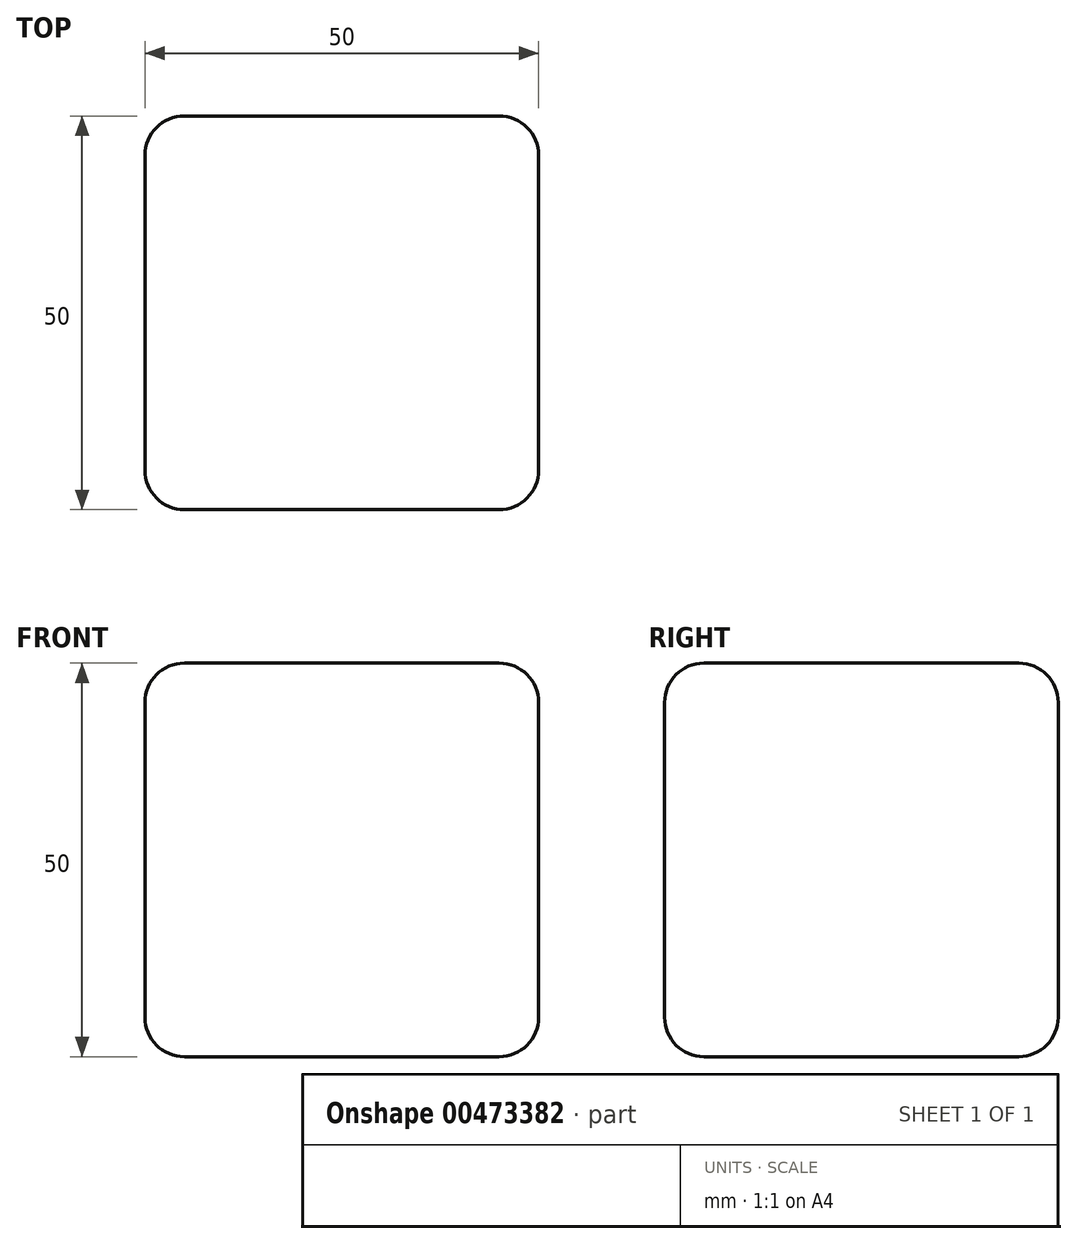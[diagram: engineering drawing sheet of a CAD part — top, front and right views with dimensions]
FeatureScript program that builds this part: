
annotation { "Feature Type Name" : "Feature", "Feature Type Description" : "" }
export const myFeature = defineFeature(function(context is Context, id is Id, definition is map)
    precondition{}
    {
        {
            var Q0;
            Q0=qCreatedBy(makeId("Front.planeOp"),FACE);
            var sketch = newSketch(context, id + "F0", { "sketchPlane" : qUnion([Q0])});
            skLineSegment(sketch, "E0.bottom", {"start": v(0, 0) * mm, "end": v(-50, 0) * mm});
            skLineSegment(sketch, "E0.top", {"start": v(0, 50) * mm, "end": v(-50, 50) * mm});
            skLineSegment(sketch, "E0.left", {"start": v(0, 0) * mm, "end": v(0, 50) * mm});
            skLineSegment(sketch, "E0.right", {"start": v(-50, 0) * mm, "end": v(-50, 50) * mm});
            skSolve(sketch);
        }
        {
            var Q0;
            Q0 = qSketchRegion(id + "F0", true);
            extrude(context, id + "F1", {"entities" : qUnion([Q0]), "depth" : 50 * mm});
        }
        {
            var Q0;
            Q0=makeQuery(id+"F1.opExtrude","SWEPT_EDGE",EDGE,{"disambiguationData":[OSD([sQuery(id+"F0.wireOp",EDGE,"E0.top"),sQuery(id+"F0.wireOp",EDGE,"E0.right")])]});
            var Q1;
            Q1=makeQuery(id+"F1.opExtrude","CAP_EDGE",EDGE,{"disambiguationData":[OSD([sQuery(id+"F0.wireOp",EDGE,"E0.top")])],"isStart":true});
            var Q2;
            Q2=makeQuery(id+"F1.opExtrude","SWEPT_EDGE",EDGE,{"disambiguationData":[OSD([sQuery(id+"F0.wireOp",EDGE,"E0.top"),sQuery(id+"F0.wireOp",EDGE,"E0.left")])]});
            var Q3;
            Q3=makeQuery(id+"F1.opExtrude","CAP_EDGE",EDGE,{"disambiguationData":[OSD([sQuery(id+"F0.wireOp",EDGE,"E0.top")])],"isStart":false});
            var Q4;
            Q4=makeQuery(id+"F1.opExtrude","CAP_EDGE",EDGE,{"disambiguationData":[OSD([sQuery(id+"F0.wireOp",EDGE,"E0.left")])],"isStart":false});
            var Q5;
            Q5=makeQuery(id+"F1.opExtrude","CAP_EDGE",EDGE,{"disambiguationData":[OSD([sQuery(id+"F0.wireOp",EDGE,"E0.left")])],"isStart":true});
            var Q6;
            Q6=makeQuery(id+"F1.opExtrude","SWEPT_EDGE",EDGE,{"disambiguationData":[OSD([sQuery(id+"F0.wireOp",EDGE,"E0.bottom"),sQuery(id+"F0.wireOp",EDGE,"E0.left")])]});
            var Q7;
            Q7=makeQuery(id+"F1.opExtrude","CAP_EDGE",EDGE,{"disambiguationData":[OSD([sQuery(id+"F0.wireOp",EDGE,"E0.bottom")])],"isStart":false});
            var Q8;
            Q8=makeQuery(id+"F1.opExtrude","CAP_EDGE",EDGE,{"disambiguationData":[OSD([sQuery(id+"F0.wireOp",EDGE,"E0.right")])],"isStart":false});
            var Q9;
            Q9=makeQuery(id+"F1.opExtrude","SWEPT_FACE",FACE,{"disambiguationData":[OSD([sQuery(id+"F0.wireOp",EDGE,"E0.right")])]});
            var Q10;
            Q10=makeQuery(id+"F1.opExtrude","CAP_EDGE",EDGE,{"disambiguationData":[OSD([sQuery(id+"F0.wireOp",EDGE,"E0.bottom")])],"isStart":true});
            fillet(context, id + "F2", {"entities" : qUnion([Q0, Q1, Q2, Q3, Q4, Q5, Q6, Q7, Q8, Q9, Q10]), "radius" : 5 * mm, "tangentPropagation" : true, "allowEdgeOverflow" : false});
        }
    });
